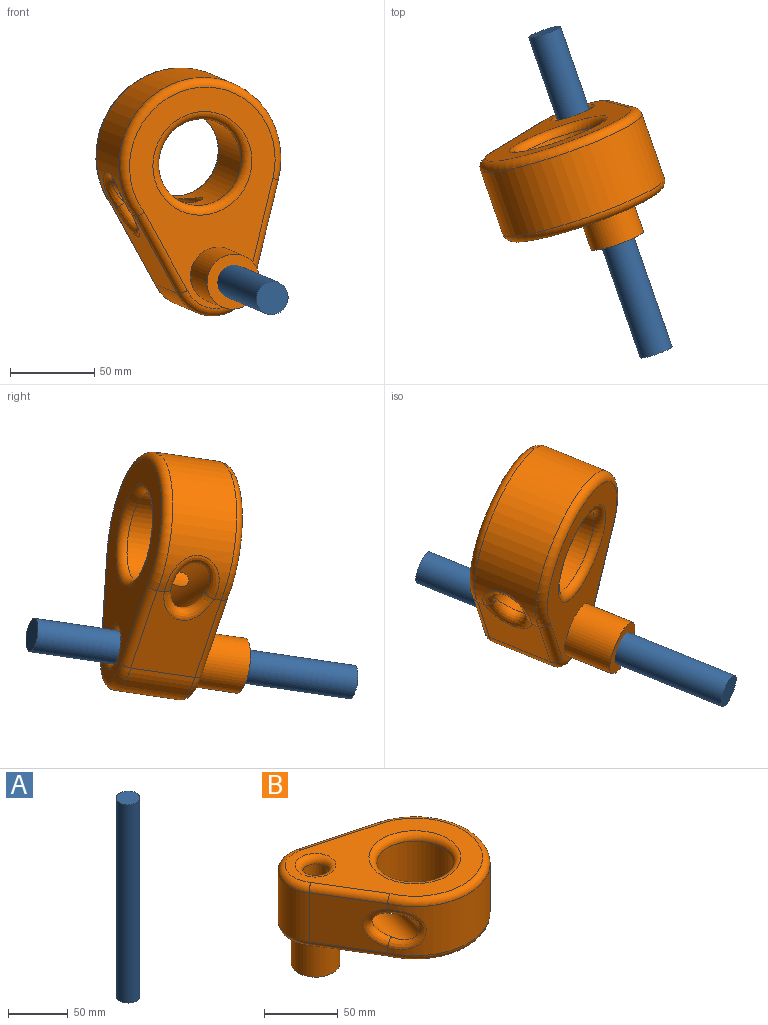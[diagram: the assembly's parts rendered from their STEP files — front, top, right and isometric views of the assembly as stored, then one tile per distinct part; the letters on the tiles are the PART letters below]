
ASSEMBLY  parts=2 mates=1
PART A: 3 faces, bbox 20x20x203.2 mm
  f0: cylinder r=10mm len=203.2mm, axis (0,0,-1), area 12767.4mm2, adj f1,f2
  f1: plane 20x20mm, normal (0,0,1), area 314.2mm2, adj f0
  f2: plane 20x20mm, normal (0,0,-1), area 314.2mm2, adj f0
PART B: 27 faces, bbox 136.7x123.3x81 mm
  f0: cylinder r=8.75mm len=75.92mm, axis (0,0,-1), area 4173.9mm2, adj f21,f26
  f1: cylinder r=16.5mm len=33mm, axis (0,0,1), area 3130.9mm2, adj f9,f26
  f2: plane 40.64x28.12mm, normal (0.26,0.97,0), area 580.9mm2, adj f6,f11,f13,f17
  f3: cylinder r=50.8mm len=99.86mm, axis (0,0,-1), area 7617.6mm2, adj f5,f7,f15,f19,f23
  f4: cylinder r=26mm len=52mm, axis (0,0,-1), area 6204.3mm2, adj f10,f12,f22
  f5: plane 40.64x30.37mm, normal (0.26,0.97,0), area 675.8mm2, adj f3,f11,f13,f17
  f6: cylinder r=25.4mm len=40.64mm, axis (0,0,-1), area 2529.2mm2, adj f2,f7,f14,f18
  f7: plane 46.65x40.64mm, normal (-0.85,-0.52,0), area 1810.7mm2, adj f3,f6,f16,f20,f23,f24
  f8: plane 120.25x106.9mm, normal (0,0,1), area 5082.9mm2, adj f17,f18,f19,f20,f21,f22
  f9: plane 120.25x106.9mm, normal (0,0,-1), area 4828.5mm2, adj f1,f12,f13,f14,f15,f16
  f10: cylinder r=11mm len=84.86mm, axis (0.26,0.97,0), area 4372.2mm2, adj f4,f23,f24,f25
  f11: cone r=11mm half-angle=45deg, axis (0.26,0.97,0), area 1147.9mm2, adj f2,f5,f13,f17,f25
  f12: torus R=31.08mm, axis (0,0,1), area 1396.1mm2, adj f4,f9
  f13: cylinder r=5.08mm len=62.11mm, axis (-0.97,0.26,0), area 502.3mm2, adj f2,f5,f9,f11,f14,f15
  f14: torus R=20.32mm, axis (0,0,1), area 461.3mm2, adj f6,f9,f13,f16
  f15: torus R=45.72mm, axis (0,0,1), area 1577.6mm2, adj f3,f9,f13,f16
  f16: cylinder r=5.08mm len=49.74mm, axis (0.52,-0.85,0), area 438mm2, adj f7,f9,f14,f15
  f17: cylinder r=5.08mm len=62.11mm, axis (0.97,-0.26,0), area 502.3mm2, adj f2,f5,f8,f11,f18,f19
  f18: torus R=20.32mm, axis (0,0,1), area 461.3mm2, adj f6,f8,f17,f20
  f19: torus R=45.72mm, axis (0,0,1), area 1577.6mm2, adj f3,f8,f17,f20
  f20: cylinder r=5.08mm len=49.74mm, axis (-0.52,0.85,0), area 438mm2, adj f7,f8,f18,f19
  f21: torus R=13.83mm, axis (0,0,1), area 531.3mm2, adj f0,f8
  f22: torus R=31.08mm, axis (0,0,1), area 1396.1mm2, adj f4,f8
  f23: bspline ~32.18x25.09mm, area 407.3mm2, adj f3,f7,f10,f24
  f24: bspline ~31.52x16.58mm, area 428.8mm2, adj f7,f10,f23
  f25: torus R=16.08mm, axis (-0.26,-0.97,0), area 288.5mm2, adj f10,f11
  f26: plane 33x33mm, normal (0,0,-1), area 614.8mm2, adj f0,f1
PLACE A rot(axis=(-0.69,-0.61,-0.4),91.3deg) t=(407.73,-549.19,-189.27)mm
PLACE B rot(axis=(-0.69,-0.61,-0.4),91.3deg) t=(370.35,-461.07,-143.45)mm
MATE slider A.f0 <-> B.f0  axis (-0.33,0.94,0.14) through (341.49,-359.14,-161.28)mm
